# Revit family: RRHS Dual Thread
name_source: partatom
category: Generic Models
revit_build: Autodesk Revit 2018 (Build: 20190510_1515(x64)
units: mm (PartAtom-declared; Revit-internal decimal feet)

## family parameters
Always vertical = No
Can host rebar = No
Cut with Voids When Loaded = No
Part Type = Normal
Room Calculation Point = No
Round Connector Dimension = Use Diameter
Shared = Yes
Work Plane-Based = Yes

## types (3) — shared parameters
Bottom Thread Diameter = 0.313 "
Bottom Thread Radius = 0.157 "
Default Elevation = 48 "
Flat Gasket = GSK002001 : GSK002001-01
Rack Slot Gasket = RRRG38
Spacer Material = <By Category>

## per-type parameters (varying)
| type | Description | Length | Taper Offset | Top Thread Diameter | Top Thread Offset | Top Thread Radius |
| RRHS38122T | Spacer Tapered Hygienic 304 Dual Threaded 3/8-16 and 1/2-13 2 Inch long | 2 " | 0.18 " | 0.422 " | 0.75 " | 0.211 " |
| RRHS38141T | Spacer Tapered Hygienic 304 Dual Threaded 3/8-16 and 1/4-20 1 Inch long | 1 " | 0.28 " | 0.201 " | 0.45 " | 0.101 " |
| RRHS38142T | Spacer Tapered Hygienic 304 Dual Threaded 3/8-16 and 1/4-20 2 Inch long | 2 " | 0.28 " | 0.201 " | 0.75 " | 0.101 " |

note: column(s) folded — value = type name in every type: Catalog Number

## geometry (parser evidence)
native form markers: Sweep x8
no freeform markers — native parametric forms only
